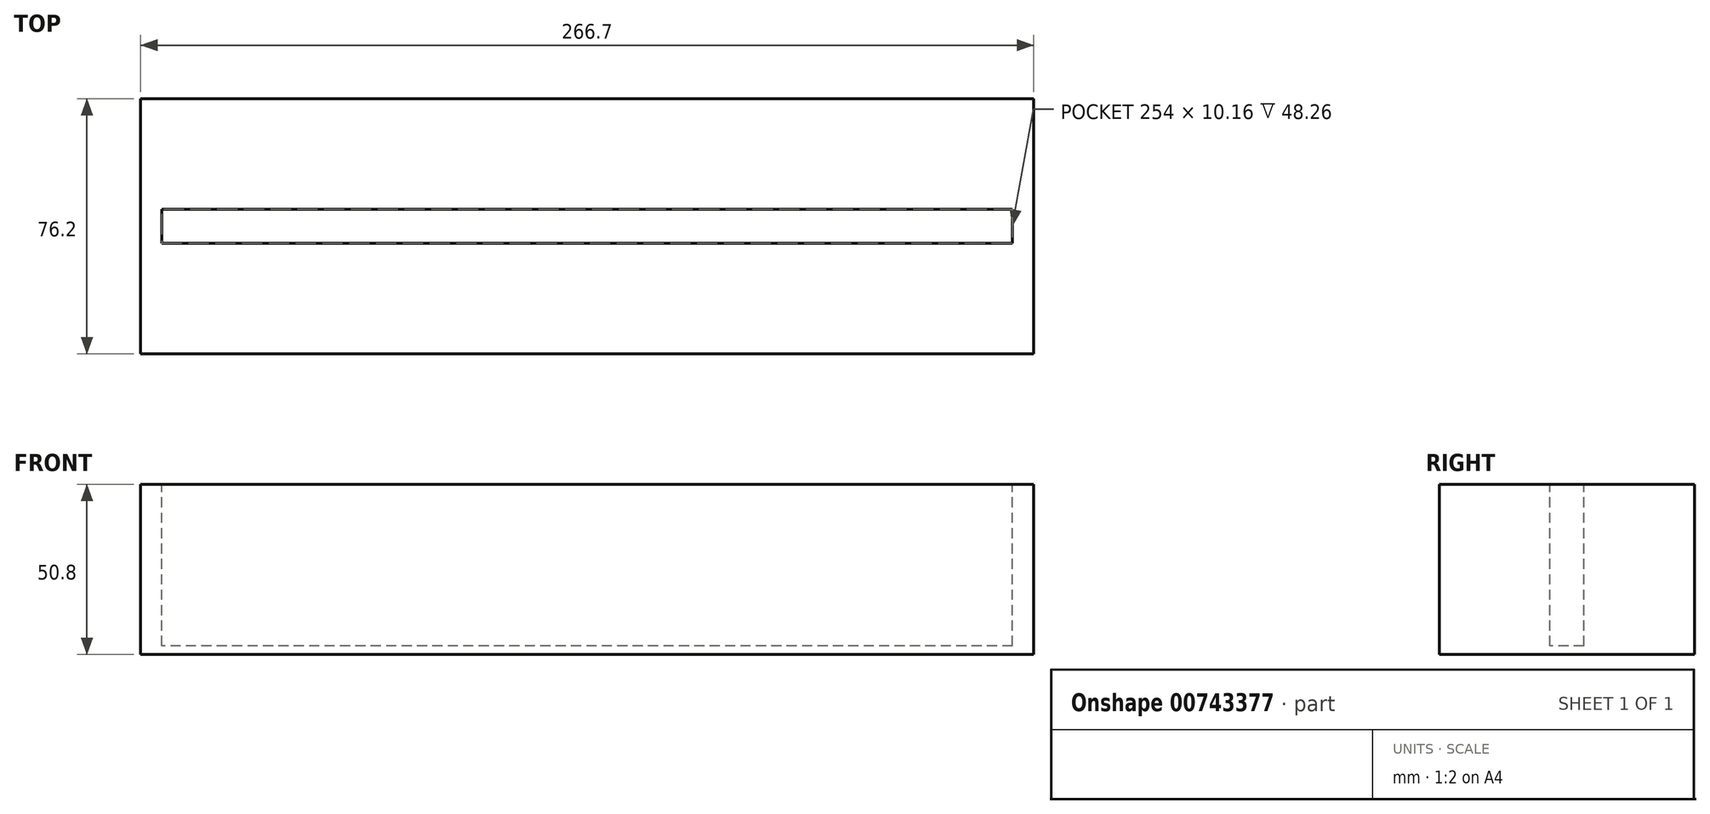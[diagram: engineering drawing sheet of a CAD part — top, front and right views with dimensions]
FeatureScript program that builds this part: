
annotation { "Feature Type Name" : "Feature", "Feature Type Description" : "" }
export const myFeature = defineFeature(function(context is Context, id is Id, definition is map)
    precondition{}
    {
        {
            var Q0;
            Q0=qCreatedBy(makeId("Front.planeOp"),FACE);
            var sketch = newSketch(context, id + "F0", { "sketchPlane" : qUnion([Q0])});
            skLineSegment(sketch, "E0.bottom", {"start": v(133.35, 25.4) * mm, "end": v(-133.35, 25.4) * mm});
            skLineSegment(sketch, "E0.top", {"start": v(133.35, -25.4) * mm, "end": v(-133.35, -25.4) * mm});
            skLineSegment(sketch, "E0.left", {"start": v(133.35, 25.4) * mm, "end": v(133.35, -25.4) * mm});
            skLineSegment(sketch, "E0.right", {"start": v(-133.35, 25.4) * mm, "end": v(-133.35, -25.4) * mm});
            skPoint(sketch, "E0.middle", {"position": v(0, 0) * mm});
            skSolve(sketch);
        }
        {
            var Q0;
            Q0=makeQuery(id+"F0.imprint","IMPRINT",FACE,{"disambiguationData":[TD([[makeQuery(id+"F0.imprint","IMPRINT",EDGE,{"derivedFrom":sQuery(id+"F0.wireOp",EDGE,"E0.bottom")}),1.0]])]});
            extrude(context, id + "F1", {"entities" : qUnion([Q0]), "endBound" : BoundingType.SYMMETRIC, "depth" : 76.2 * mm, "offsetDistance" : 25.4 * mm});
        }
        {
            var Q0;
            Q0=makeQuery(id+"F1.opExtrude","SWEPT_FACE",FACE,{"disambiguationData":[OSD([sQuery(id+"F0.wireOp",EDGE,"E0.bottom")])]});
            var sketch = newSketch(context, id + "F2", { "sketchPlane" : qUnion([Q0])});
            skLineSegment(sketch, "E1.bottom", {"start": v(127, 5.08) * mm, "end": v(-127, 5.08) * mm});
            skLineSegment(sketch, "E1.top", {"start": v(127, -5.08) * mm, "end": v(-127, -5.08) * mm});
            skLineSegment(sketch, "E1.left", {"start": v(127, 5.08) * mm, "end": v(127, -5.08) * mm});
            skLineSegment(sketch, "E1.right", {"start": v(-127, 5.08) * mm, "end": v(-127, -5.08) * mm});
            skPoint(sketch, "E1.middle", {"position": v(0, 0) * mm});
            skSolve(sketch);
        }
        {
            var Q0;
            Q0 = qSketchRegion(id + "F2", true);
            extrude(context, id + "F3", {"entities" : qUnion([Q0]), "operationType" : NewBodyOperationType.REMOVE, "oppositeDirection" : true, "depth" : 48.26 * mm, "offsetDistance" : 25.4 * mm});
        }
    });
